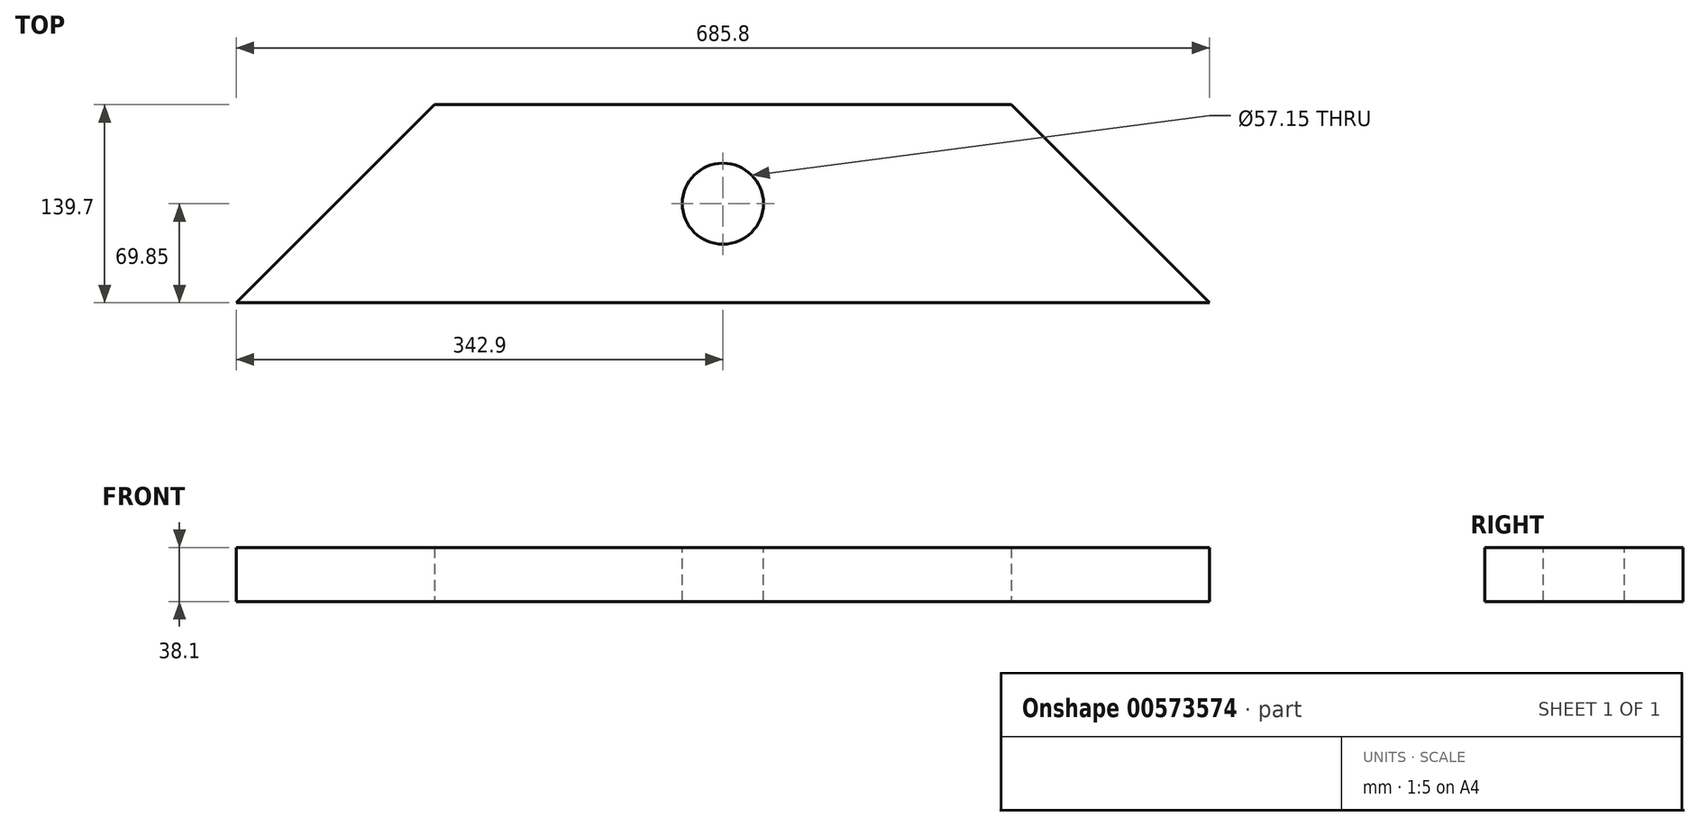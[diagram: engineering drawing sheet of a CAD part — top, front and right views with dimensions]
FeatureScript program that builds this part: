
annotation { "Feature Type Name" : "Feature", "Feature Type Description" : "" }
export const myFeature = defineFeature(function(context is Context, id is Id, definition is map)
    precondition{}
    {
        {
            var Q0;
            Q0=qCreatedBy(makeId("Top.planeOp"),FACE);
            var sketch = newSketch(context, id + "F0", { "sketchPlane" : qUnion([Q0])});
            skLineSegment(sketch, "E0.bottom", {"start": v(203.2, 69.85) * mm, "end": v(-203.2, 69.85) * mm});
            skLineSegment(sketch, "E0.top", {"start": v(203.2, -69.85) * mm, "end": v(-203.2, -69.85) * mm, "construction": true});
            skPoint(sketch, "E0.middle", {"position": v(0, 0) * mm});
            skLineSegment(sketch, "E1", {"start": v(203.2, -69.85) * mm, "end": v(382.2, -69.85) * mm, "construction": true});
            skLineSegment(sketch, "E2", {"start": v(-203.2, -69.85) * mm, "end": v(-356.6, -69.85) * mm, "construction": true});
            skLineSegment(sketch, "E3", {"start": v(-203.2, 69.85) * mm, "end": v(-342.9, -69.85) * mm});
            skLineSegment(sketch, "E4", {"start": v(-342.9, -69.85) * mm, "end": v(342.9, -69.85) * mm});
            skLineSegment(sketch, "E5", {"start": v(342.9, -69.85) * mm, "end": v(203.2, 69.85) * mm});
            skSolve(sketch);
        }
        {
            var Q0;
            Q0 = qSketchRegion(id + "F0", true);
            extrude(context, id + "F1", {"entities" : qUnion([Q0]), "depth" : 38.1 * mm, "offsetDistance" : 25.4 * mm});
        }
        {
            var Q0;
            Q0=makeQuery(id+"F1.opExtrude","CAP_FACE",FACE,{"disambiguationData":[OSD([sQuery(id+"F0.wireOp",EDGE,"E0.bottom"),sQuery(id+"F0.wireOp",EDGE,"E3"),sQuery(id+"F0.wireOp",EDGE,"E4"),sQuery(id+"F0.wireOp",EDGE,"E5")])],"isStart":false});
            var sketch = newSketch(context, id + "F2", { "sketchPlane" : qUnion([Q0])});
            skCircle(sketch, "E6", {"center": v(0, 0) * mm, "radius": 28.58 * mm});
            skSolve(sketch);
        }
        {
            var Q0;
            Q0 = qSketchRegion(id + "F2", true);
            extrude(context, id + "F3", {"entities" : qUnion([Q0]), "operationType" : NewBodyOperationType.REMOVE, "endBound" : BoundingType.THROUGH_ALL, "oppositeDirection" : true, "depth" : 25.4 * mm, "offsetDistance" : 25.4 * mm});
        }
    });
